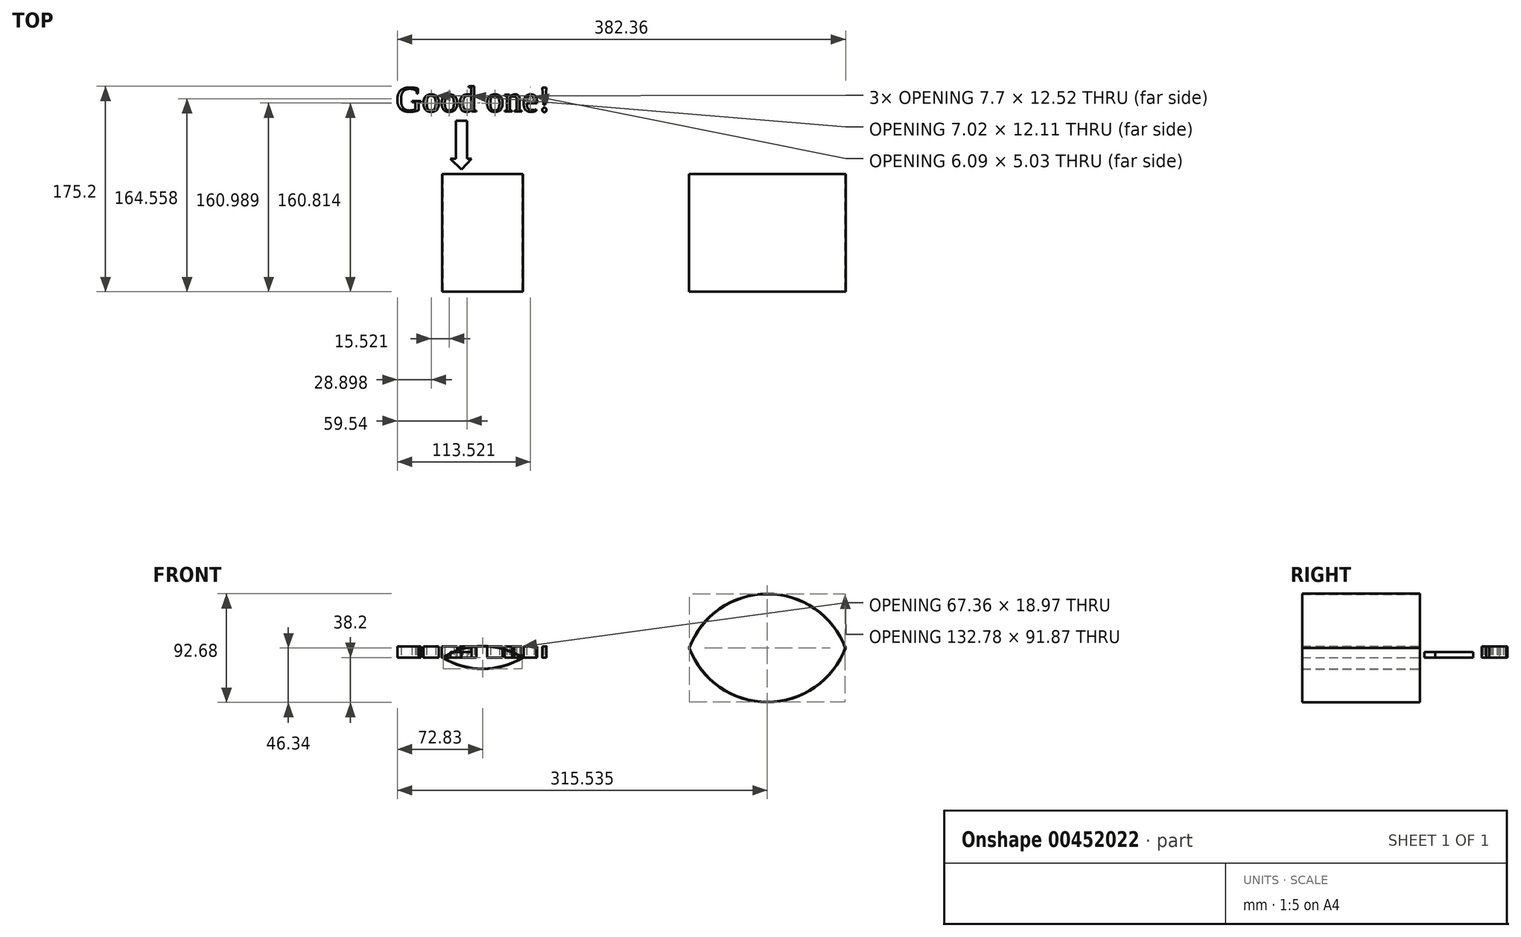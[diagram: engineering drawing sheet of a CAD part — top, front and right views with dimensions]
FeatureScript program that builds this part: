
annotation { "Feature Type Name" : "Feature", "Feature Type Description" : "" }
export const myFeature = defineFeature(function(context is Context, id is Id, definition is map)
    precondition{}
    {
        {
            var Q0;
            Q0=qCreatedBy(makeId("Front.planeOp"),FACE);
            var sketch = newSketch(context, id + "F0", { "sketchPlane" : qUnion([Q0])});
            skLineSegment(sketch, "E0", {"start": v(161.11, 89.53) * mm, "end": v(161.11, -76.05) * mm, "construction": true});
            skArc(sketch, "E1", {"start": v(227.5, 8.14) * mm, "mid": v(161.11, 54.08) * mm, "end": v(94.73, 8.14) * mm});
            skArc(sketch, "E2", {"start": v(227.5, 8.14) * mm, "mid": v(161.11, -37.8) * mm, "end": v(94.73, 8.14) * mm});
            skArc(sketch, "E3.0", {"start": v(227.94, 8.14) * mm, "mid": v(161.11, 54.48) * mm, "end": v(94.3, 8.14) * mm});
            skArc(sketch, "E3.1", {"start": v(227.94, 8.14) * mm, "mid": v(161.11, -38.2) * mm, "end": v(94.3, 8.14) * mm});
            skSolve(sketch);
        }
        {
            var Q0;
            Q0 = qSketchRegion(id + "F0", true);
            extrude(context, id + "F1", {"entities" : qUnion([Q0]), "depth" : 100.25 * mm, "offsetDistance" : 25.4 * mm});
        }
        {
            var Q0;
            Q0=qCreatedBy(makeId("Front.planeOp"),FACE);
            var sketch = newSketch(context, id + "F2", { "sketchPlane" : qUnion([Q0])});
            skLineSegment(sketch, "E4", {"start": v(-81.59, 68.77) * mm, "end": v(-81.59, -47.25) * mm, "construction": true});
            skArc(sketch, "E5", {"start": v(-47.91, 0) * mm, "mid": v(-81.59, 9.48) * mm, "end": v(-115.27, 0) * mm});
            skArc(sketch, "E6", {"start": v(-47.91, 0) * mm, "mid": v(-81.59, -9.48) * mm, "end": v(-115.27, 0) * mm});
            skArc(sketch, "E7.0", {"start": v(-47.14, 0) * mm, "mid": v(-81.59, 9.9) * mm, "end": v(-116.04, 0) * mm});
            skArc(sketch, "E7.1", {"start": v(-47.14, 0) * mm, "mid": v(-81.59, -9.9) * mm, "end": v(-116.04, 0) * mm});
            skSolve(sketch);
        }
        {
            var Q0;
            Q0 = qSketchRegion(id + "F2", true);
            extrude(context, id + "F3", {"entities" : qUnion([Q0]), "depth" : 100.28 * mm, "offsetDistance" : 25.4 * mm});
        }
        {
            var Q0;
            Q0=qCreatedBy(makeId("Top.planeOp"),FACE);
            var sketch = newSketch(context, id + "F4", { "sketchPlane" : qUnion([Q0])});
            skText(sketch, "E8", { "text": "Good one!", "fontName": "Tinos-Regular.ttf"});
            const initialGuessF4  = {"E8": [-0.1557, 0.05338, 1, 0, 0.02235]};
            skSetInitialGuess(sketch, initialGuessF4);
            skSolve(sketch);
        }
        {
            var Q0;
            Q0 = qSketchRegion(id + "F4", true);
            extrude(context, id + "F5", {"entities" : qUnion([Q0]), "depth" : 9.6 * mm, "offsetDistance" : 25.4 * mm});
        }
        {
            var Q0;
            Q0=qCreatedBy(makeId("Top.planeOp"),FACE);
            var sketch = newSketch(context, id + "F6", { "sketchPlane" : qUnion([Q0])});
            skLineSegment(sketch, "E9.bottom", {"start": v(-104.47, 45.48) * mm, "end": v(-94.82, 45.48) * mm});
            skLineSegment(sketch, "E9.top", {"start": v(-104.47, 13.05) * mm, "end": v(-94.82, 13.05) * mm});
            skLineSegment(sketch, "E9.left", {"start": v(-104.47, 45.48) * mm, "end": v(-104.47, 13.05) * mm});
            skLineSegment(sketch, "E9.right", {"start": v(-94.82, 45.48) * mm, "end": v(-94.82, 13.05) * mm});
            skLineSegment(sketch, "E10", {"start": v(-104.47, 13.05) * mm, "end": v(-109.19, 13.05) * mm});
            skLineSegment(sketch, "E11", {"start": v(-109.19, 13.05) * mm, "end": v(-99.65, 3.94) * mm});
            skPoint(sketch, "E11.endSnap0", {"position": v(-99.65, 13.05) * mm});
            skLineSegment(sketch, "E12", {"start": v(-99.65, 3.94) * mm, "end": v(-90.95, 13.05) * mm});
            skLineSegment(sketch, "E13", {"start": v(-90.95, 13.05) * mm, "end": v(-94.82, 13.05) * mm});
            skSolve(sketch);
        }
        {
            var Q0;
            Q0 = qSketchRegion(id + "F6", true);
            extrude(context, id + "F7", {"entities" : qUnion([Q0]), "depth" : 4.76 * mm, "offsetDistance" : 25.4 * mm});
        }
    });
